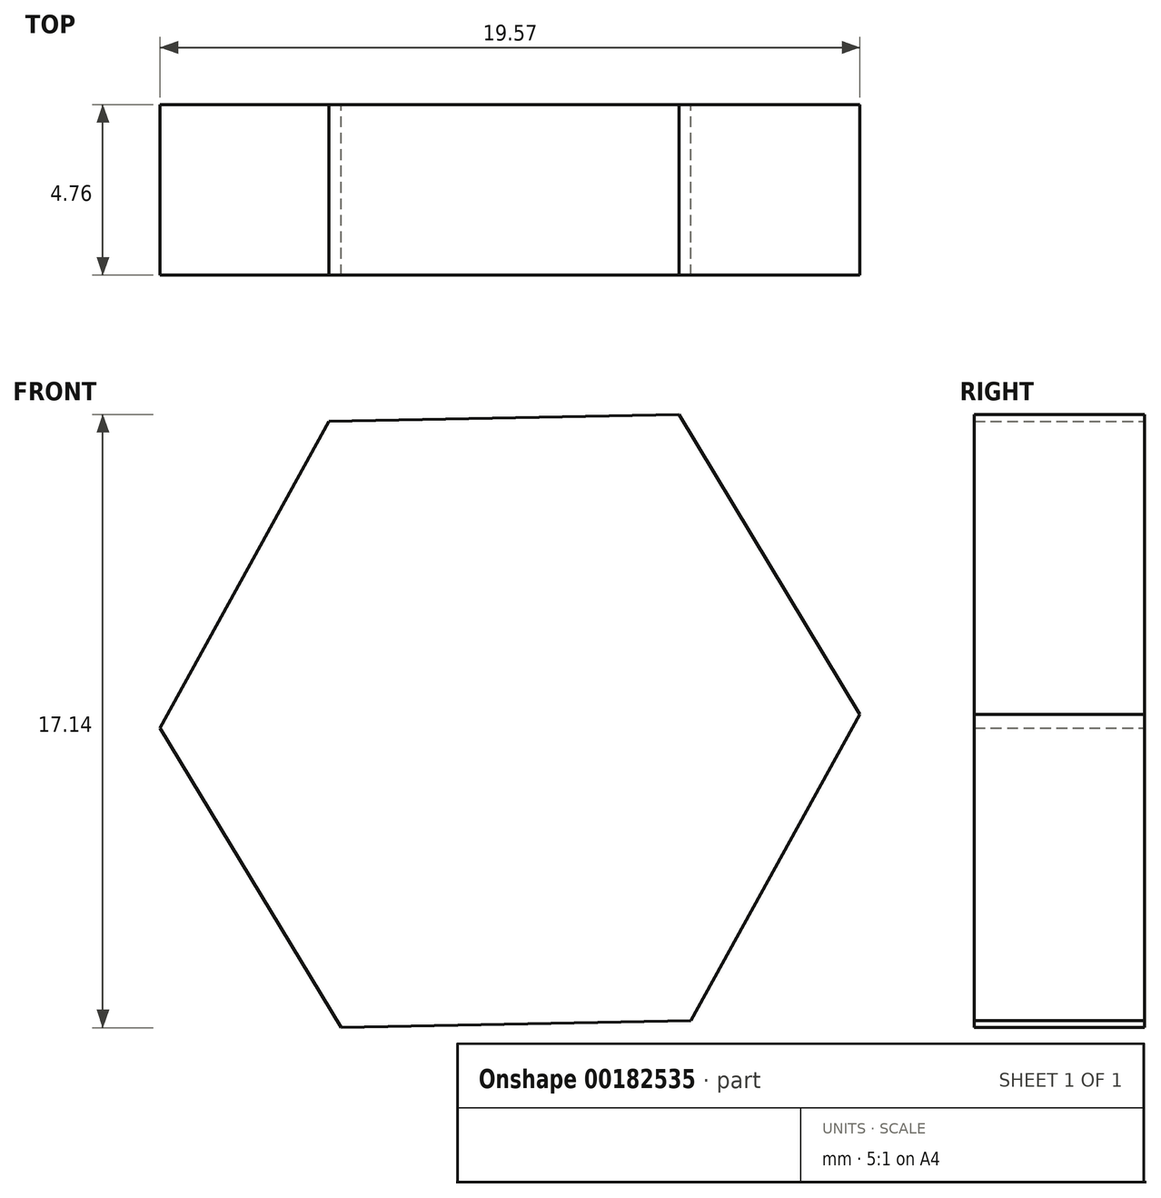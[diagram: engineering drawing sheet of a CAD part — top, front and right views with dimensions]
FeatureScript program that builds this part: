
annotation { "Feature Type Name" : "Feature", "Feature Type Description" : "" }
export const myFeature = defineFeature(function(context is Context, id is Id, definition is map)
    precondition{}
    {
        {
            var Q0;
            Q0=qCreatedBy(makeId("Front.planeOp"),FACE);
            var sketch = newSketch(context, id + "F0", { "sketchPlane" : qUnion([Q0])});
            skCircle(sketch, "E0.cCircle", {"center": v(-8.16, 7.59) * mm, "radius": 8.47 * mm, "construction": true});
            skLineSegment(sketch, "E0.0", {"start": v(1.63, 7.78) * mm, "end": v(-3.1, -0.79) * mm});
            skLineSegment(sketch, "E0.1", {"start": v(-3.1, -0.79) * mm, "end": v(-12.88, -0.98) * mm});
            skLineSegment(sketch, "E0.2", {"start": v(-12.88, -0.98) * mm, "end": v(-17.94, 7.4) * mm});
            skLineSegment(sketch, "E0.3", {"start": v(-17.94, 7.4) * mm, "end": v(-13.21, 15.97) * mm});
            skLineSegment(sketch, "E0.4", {"start": v(-13.21, 15.97) * mm, "end": v(-3.43, 16.16) * mm});
            skLineSegment(sketch, "E0.5", {"start": v(-3.43, 16.16) * mm, "end": v(1.63, 7.78) * mm});
            skPoint(sketch, "E0.0.midPoint", {"position": v(-0.74, 3.5) * mm});
            skSolve(sketch);
        }
        {
            var Q0;
            Q0=makeQuery(id+"F0.imprint","IMPRINT",FACE,{"disambiguationData":[TD([[makeQuery(id+"F0.imprint","IMPRINT",EDGE,{"derivedFrom":sQuery(id+"F0.wireOp",EDGE,"E0.0")}),-1.0]])]});
            extrude(context, id + "F1", {"entities" : qUnion([Q0]), "depth" : 4.76 * mm});
        }
    });
